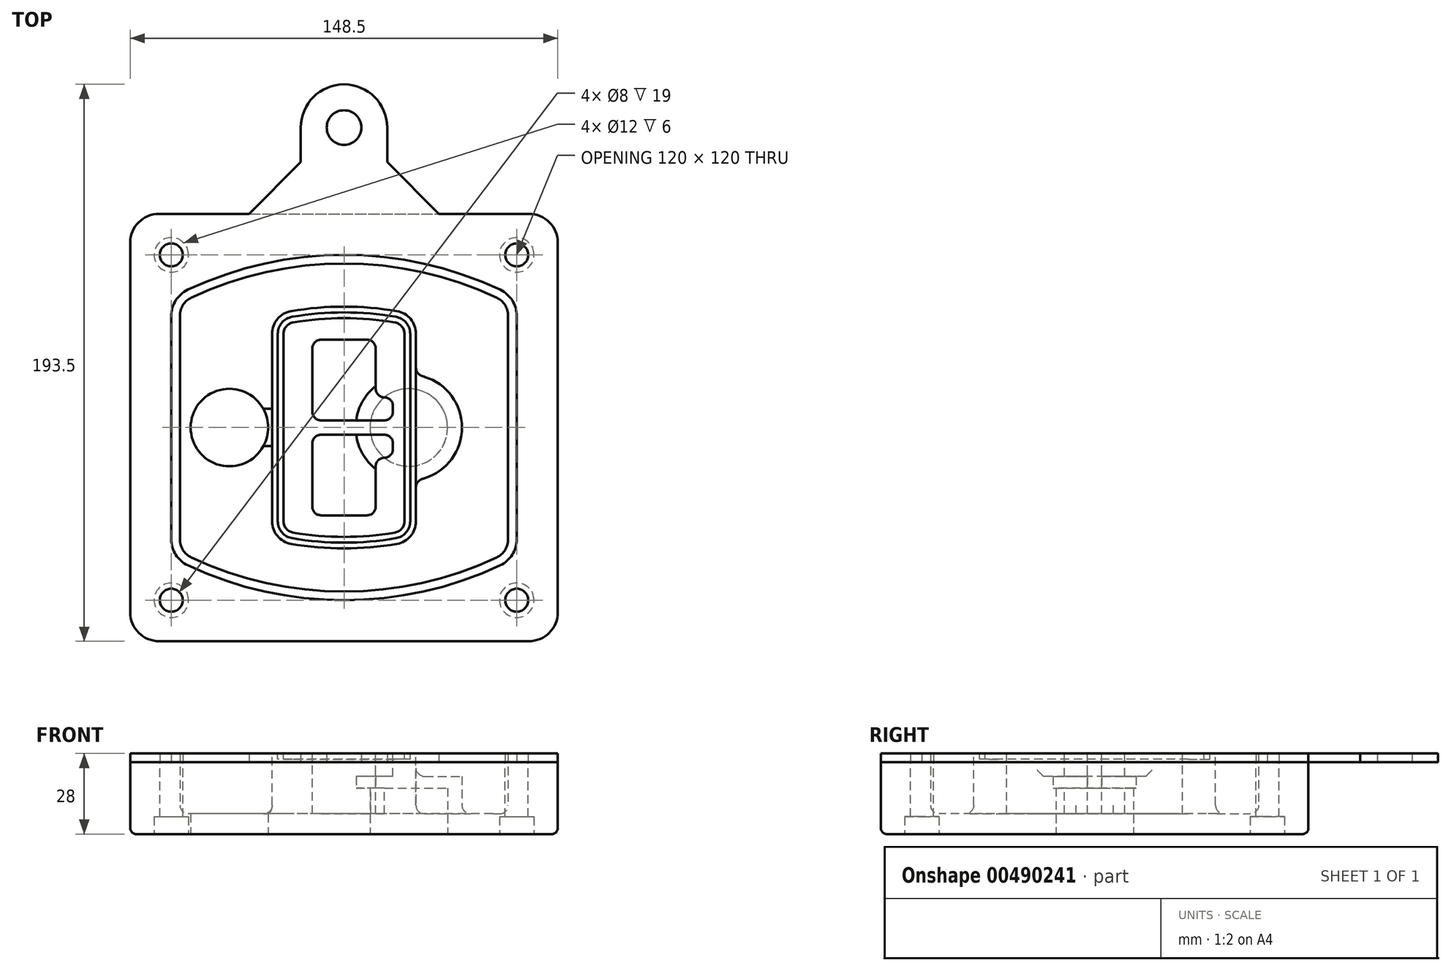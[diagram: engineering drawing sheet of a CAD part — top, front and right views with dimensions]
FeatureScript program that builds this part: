
annotation { "Feature Type Name" : "Feature", "Feature Type Description" : "" }
export const myFeature = defineFeature(function(context is Context, id is Id, definition is map)
    precondition{}
    {
        {
            var Q0;
            Q0=qCreatedBy(makeId("Top.planeOp"),FACE);
            var sketch = newSketch(context, id + "F0", { "sketchPlane" : qUnion([Q0])});
            skPoint(sketch, "E0.rect.middle", {"position": v(0, 0) * mm});
            skLineSegment(sketch, "E1.bottom", {"start": v(-64.25, -74.25) * mm, "end": v(64.25, -74.25) * mm});
            skLineSegment(sketch, "E1.top", {"start": v(-64.25, 74.25) * mm, "end": v(64.25, 74.25) * mm});
            skLineSegment(sketch, "E1.left", {"start": v(-74.25, -64.25) * mm, "end": v(-74.25, 64.25) * mm});
            skLineSegment(sketch, "E1.right", {"start": v(74.25, -64.25) * mm, "end": v(74.25, 64.25) * mm});
            skLineSegment(sketch, "E2", {"start": v(-74.25, 74.25) * mm, "end": v(74.25, -74.25) * mm, "construction": true});
            skLineSegment(sketch, "E3", {"start": v(74.25, 74.25) * mm, "end": v(-74.25, -74.25) * mm, "construction": true});
            skCircle(sketch, "E4", {"center": v(-60, 60) * mm, "radius": 4 * mm});
            skCircle(sketch, "E5", {"center": v(60, 60) * mm, "radius": 4 * mm});
            skCircle(sketch, "E6", {"center": v(60, -60) * mm, "radius": 4 * mm});
            skCircle(sketch, "E7", {"center": v(-60, -60) * mm, "radius": 4 * mm});
            skLineSegment(sketch, "E8", {"start": v(-60, 60) * mm, "end": v(60, 60) * mm, "construction": true});
            skLineSegment(sketch, "E9", {"start": v(60, 60) * mm, "end": v(60, -60) * mm, "construction": true});
            skLineSegment(sketch, "E10", {"start": v(60, -60) * mm, "end": v(-60, -60) * mm, "construction": true});
            skLineSegment(sketch, "E11", {"start": v(-60, -60) * mm, "end": v(-60, 60) * mm, "construction": true});
            skLineSegment(sketch, "E12", {"start": v(-60, 38.83) * mm, "end": v(-60, -38.83) * mm});
            skLineSegment(sketch, "E13", {"start": v(60, 38.83) * mm, "end": v(60, -38.83) * mm});
            skArc(sketch, "E14", {"start": v(54.26, 47.88) * mm, "mid": v(0, 60) * mm, "end": v(-54.26, 47.88) * mm});
            skArc(sketch, "E15", {"start": v(-54.26, -47.88) * mm, "mid": v(0, -60) * mm, "end": v(54.26, -47.88) * mm});
            skLineSegment(sketch, "E16", {"start": v(-60, 0) * mm, "end": v(60, 0) * mm, "construction": true});
            skPoint(sketch, "E17.visualSharp", {"position": v(-60, -45) * mm});
            skArc(sketch, "E17.filletArc", {"start": v(-60, -38.83) * mm, "mid": v(-58.44, -44.2) * mm, "end": v(-54.26, -47.88) * mm});
            skPoint(sketch, "E18.visualSharp", {"position": v(-60, 45) * mm});
            skArc(sketch, "E18.filletArc", {"start": v(-54.26, 47.88) * mm, "mid": v(-58.44, 44.2) * mm, "end": v(-60, 38.83) * mm});
            skPoint(sketch, "E19.visualSharp", {"position": v(60, 45) * mm});
            skArc(sketch, "E19.filletArc", {"start": v(60, 38.83) * mm, "mid": v(58.44, 44.2) * mm, "end": v(54.26, 47.88) * mm});
            skPoint(sketch, "E20.visualSharp", {"position": v(60, -45) * mm});
            skArc(sketch, "E20.filletArc", {"start": v(54.26, -47.88) * mm, "mid": v(58.44, -44.2) * mm, "end": v(60, -38.83) * mm});
            skPoint(sketch, "E21.visualSharp", {"position": v(-74.25, 74.25) * mm});
            skArc(sketch, "E21.filletArc", {"start": v(-64.25, 74.25) * mm, "mid": v(-71.32, 71.32) * mm, "end": v(-74.25, 64.25) * mm});
            skPoint(sketch, "E22.visualSharp", {"position": v(74.25, 74.25) * mm});
            skArc(sketch, "E22.filletArc", {"start": v(74.25, 64.25) * mm, "mid": v(71.32, 71.32) * mm, "end": v(64.25, 74.25) * mm});
            skPoint(sketch, "E23.visualSharp", {"position": v(74.25, -74.25) * mm});
            skArc(sketch, "E23.filletArc", {"start": v(64.25, -74.25) * mm, "mid": v(71.32, -71.32) * mm, "end": v(74.25, -64.25) * mm});
            skPoint(sketch, "E24.visualSharp", {"position": v(-74.25, -74.25) * mm});
            skArc(sketch, "E24.filletArc", {"start": v(-74.25, -64.25) * mm, "mid": v(-71.32, -71.32) * mm, "end": v(-64.25, -74.25) * mm});
            skArc(sketch, "E25.0", {"start": v(57, 38.83) * mm, "mid": v(55.9, 42.58) * mm, "end": v(52.98, 45.17) * mm});
            skLineSegment(sketch, "E25.1", {"start": v(57, 38.83) * mm, "end": v(57, -38.83) * mm});
            skArc(sketch, "E25.2", {"start": v(52.98, -45.17) * mm, "mid": v(55.9, -42.58) * mm, "end": v(57, -38.83) * mm});
            skArc(sketch, "E25.3", {"start": v(-52.98, -45.17) * mm, "mid": v(0, -57) * mm, "end": v(52.98, -45.17) * mm});
            skArc(sketch, "E25.4", {"start": v(-57, -38.83) * mm, "mid": v(-55.9, -42.58) * mm, "end": v(-52.98, -45.17) * mm});
            skArc(sketch, "E25.5", {"start": v(52.98, 45.17) * mm, "mid": v(0, 57) * mm, "end": v(-52.98, 45.17) * mm});
            skLineSegment(sketch, "E25.6", {"start": v(-57, 38.83) * mm, "end": v(-57, -38.83) * mm});
            skArc(sketch, "E25.7", {"start": v(-52.98, 45.17) * mm, "mid": v(-55.9, 42.58) * mm, "end": v(-57, 38.83) * mm});
            skArc(sketch, "E26.0", {"start": v(-55.96, 51.5) * mm, "mid": v(-61.82, 46.33) * mm, "end": v(-64, 38.83) * mm});
            skArc(sketch, "E26.1", {"start": v(55.96, 51.5) * mm, "mid": v(0, 64) * mm, "end": v(-55.96, 51.5) * mm});
            skArc(sketch, "E26.2", {"start": v(64, 38.83) * mm, "mid": v(61.82, 46.33) * mm, "end": v(55.96, 51.5) * mm});
            skLineSegment(sketch, "E26.3", {"start": v(64, 38.83) * mm, "end": v(64, -38.83) * mm});
            skArc(sketch, "E26.4", {"start": v(55.96, -51.5) * mm, "mid": v(61.82, -46.33) * mm, "end": v(64, -38.83) * mm});
            skLineSegment(sketch, "E26.5", {"start": v(-64, 38.83) * mm, "end": v(-64, -38.83) * mm});
            skArc(sketch, "E26.6", {"start": v(-55.96, -51.5) * mm, "mid": v(0, -64) * mm, "end": v(55.96, -51.5) * mm});
            skArc(sketch, "E26.7", {"start": v(-64, -38.83) * mm, "mid": v(-61.82, -46.33) * mm, "end": v(-55.96, -51.5) * mm});
            skSolve(sketch);
        }
        {
            var Q0;
            Q0=makeQuery(id+"F0.imprint","IMPRINT",FACE,{"disambiguationData":[TD([[makeQuery(id+"F0.imprint","IMPRINT",EDGE,{"derivedFrom":sQuery(id+"F0.wireOp",EDGE,"E1.bottom")}),1.0]])]});
            var Q1;
            Q1=makeQuery(id+"F0.imprint","IMPRINT",FACE,{"disambiguationData":[TD([[makeQuery(id+"F0.imprint","IMPRINT",EDGE,{"derivedFrom":sQuery(id+"F0.wireOp",EDGE,"E12")}),1.0]])]});
            var Q2;
            Q2=makeQuery(id+"F0.imprint","IMPRINT",FACE,{"disambiguationData":[TD([[makeQuery(id+"F0.imprint","IMPRINT",EDGE,{"derivedFrom":sQuery(id+"F0.wireOp",EDGE,"E25.0")}),1.0]])]});
            var Q3;
            Q3=makeQuery(id+"F0.imprint","IMPRINT",FACE,{"disambiguationData":[TD([[makeQuery(id+"F0.imprint","IMPRINT",EDGE,{"derivedFrom":sQuery(id+"F0.wireOp",EDGE,"E12")}),-1.0]])]});
            extrude(context, id + "F1", {"entities" : qUnion([Q0, Q1, Q2, Q3]), "oppositeDirection" : true, "depth" : 25 * mm});
        }
        {
            var Q0;
            Q0=makeQuery(id+"F0.imprint","IMPRINT",FACE,{"disambiguationData":[TD([[makeQuery(id+"F0.imprint","IMPRINT",EDGE,{"derivedFrom":sQuery(id+"F0.wireOp",EDGE,"E12")}),1.0]])]});
            extrude(context, id + "F2", {"entities" : qUnion([Q0]), "operationType" : NewBodyOperationType.ADD, "depth" : 3 * mm});
        }
        {
            var Q0;
            Q0=makeQuery(id+"F0.imprint","IMPRINT",FACE,{"disambiguationData":[TD([[makeQuery(id+"F0.imprint","IMPRINT",EDGE,{"derivedFrom":sQuery(id+"F0.wireOp",EDGE,"E25.0")}),1.0]])]});
            extrude(context, id + "F3", {"entities" : qUnion([Q0]), "operationType" : NewBodyOperationType.REMOVE, "oppositeDirection" : true, "depth" : 18 * mm});
        }
        {
            var Q0;
            Q0=makeQuery(id+"F2.opExtrude","CAP_FACE",FACE,{"disambiguationData":[OSD([sQuery(id+"F0.wireOp",EDGE,"E12"),sQuery(id+"F0.wireOp",EDGE,"E13"),sQuery(id+"F0.wireOp",EDGE,"E14"),sQuery(id+"F0.wireOp",EDGE,"E15"),sQuery(id+"F0.wireOp",EDGE,"E17.filletArc"),sQuery(id+"F0.wireOp",EDGE,"E18.filletArc"),sQuery(id+"F0.wireOp",EDGE,"E19.filletArc"),sQuery(id+"F0.wireOp",EDGE,"E20.filletArc"),sQuery(id+"F0.wireOp",EDGE,"E25.0"),sQuery(id+"F0.wireOp",EDGE,"E25.1"),sQuery(id+"F0.wireOp",EDGE,"E25.2"),sQuery(id+"F0.wireOp",EDGE,"E25.3"),sQuery(id+"F0.wireOp",EDGE,"E25.4"),sQuery(id+"F0.wireOp",EDGE,"E25.5"),sQuery(id+"F0.wireOp",EDGE,"E25.6"),sQuery(id+"F0.wireOp",EDGE,"E25.7")])],"isStart":false});
            var sketch = newSketch(context, id + "F4", { "sketchPlane" : qUnion([Q0])});
            skArc(sketch, "E27.0", {"start": v(-18.34, -40.45) * mm, "mid": v(0, -42) * mm, "end": v(18.34, -40.45) * mm});
            skArc(sketch, "E28.0", {"start": v(18.34, 40.45) * mm, "mid": v(0, 42) * mm, "end": v(-18.34, 40.45) * mm});
            skLineSegment(sketch, "E29", {"start": v(-25, 32.57) * mm, "end": v(-25, -32.57) * mm});
            skLineSegment(sketch, "E30", {"start": v(25, 32.57) * mm, "end": v(25, -32.57) * mm});
            skLineSegment(sketch, "E31", {"start": v(-25, 39.1) * mm, "end": v(25, 39.1) * mm, "construction": true});
            skLineSegment(sketch, "E32", {"start": v(-25, -39.1) * mm, "end": v(25, -39.1) * mm, "construction": true});
            skPoint(sketch, "E33.visualSharp", {"position": v(-25, 39.1) * mm});
            skArc(sketch, "E33.filletArc", {"start": v(-18.34, 40.45) * mm, "mid": v(-23.11, 37.73) * mm, "end": v(-25, 32.57) * mm});
            skPoint(sketch, "E34.visualSharp", {"position": v(25, 39.1) * mm});
            skArc(sketch, "E34.filletArc", {"start": v(25, 32.57) * mm, "mid": v(23.11, 37.73) * mm, "end": v(18.34, 40.45) * mm});
            skPoint(sketch, "E35.visualSharp", {"position": v(25, -39.1) * mm});
            skArc(sketch, "E35.filletArc", {"start": v(18.34, -40.45) * mm, "mid": v(23.11, -37.73) * mm, "end": v(25, -32.57) * mm});
            skPoint(sketch, "E36.visualSharp", {"position": v(-25, -39.1) * mm});
            skArc(sketch, "E36.filletArc", {"start": v(-25, -32.57) * mm, "mid": v(-23.11, -37.73) * mm, "end": v(-18.34, -40.45) * mm});
            skArc(sketch, "E37.0", {"start": v(52.98, 45.17) * mm, "mid": v(0, 57) * mm, "end": v(-52.98, 45.17) * mm});
            skArc(sketch, "E37.1", {"start": v(-52.98, 45.17) * mm, "mid": v(-55.9, 42.58) * mm, "end": v(-57, 38.83) * mm});
            skLineSegment(sketch, "E37.2", {"start": v(-57, 38.83) * mm, "end": v(-57, -38.83) * mm});
            skArc(sketch, "E37.3", {"start": v(-57, -38.83) * mm, "mid": v(-55.9, -42.58) * mm, "end": v(-52.98, -45.17) * mm});
            skArc(sketch, "E37.4", {"start": v(-52.98, -45.17) * mm, "mid": v(0, -57) * mm, "end": v(52.98, -45.17) * mm});
            skArc(sketch, "E37.5", {"start": v(52.98, -45.17) * mm, "mid": v(55.9, -42.58) * mm, "end": v(57, -38.83) * mm});
            skLineSegment(sketch, "E37.6", {"start": v(57, 38.83) * mm, "end": v(57, -38.83) * mm});
            skArc(sketch, "E37.7", {"start": v(57, 38.83) * mm, "mid": v(55.9, 42.58) * mm, "end": v(52.98, 45.17) * mm});
            skLineSegment(sketch, "E38.0", {"start": v(23, 32.57) * mm, "end": v(23, -32.57) * mm});
            skArc(sketch, "E38.1", {"start": v(18, -38.48) * mm, "mid": v(21.58, -36.44) * mm, "end": v(23, -32.57) * mm});
            skArc(sketch, "E38.2", {"start": v(-18, -38.48) * mm, "mid": v(0, -40) * mm, "end": v(18, -38.48) * mm});
            skArc(sketch, "E38.3", {"start": v(-23, -32.57) * mm, "mid": v(-21.58, -36.44) * mm, "end": v(-18, -38.48) * mm});
            skLineSegment(sketch, "E38.4", {"start": v(-23, 32.57) * mm, "end": v(-23, -32.57) * mm});
            skArc(sketch, "E38.5", {"start": v(23, 32.57) * mm, "mid": v(21.58, 36.44) * mm, "end": v(18, 38.48) * mm});
            skArc(sketch, "E38.6", {"start": v(-18, 38.48) * mm, "mid": v(-21.58, 36.44) * mm, "end": v(-23, 32.57) * mm});
            skArc(sketch, "E38.7", {"start": v(18, 38.48) * mm, "mid": v(0, 40) * mm, "end": v(-18, 38.48) * mm});
            skArc(sketch, "E39.0", {"start": v(21, 32.57) * mm, "mid": v(20.06, 35.15) * mm, "end": v(17.67, 36.5) * mm});
            skLineSegment(sketch, "E39.1", {"start": v(21, 32.57) * mm, "end": v(21, -32.57) * mm});
            skArc(sketch, "E39.2", {"start": v(17.67, -36.5) * mm, "mid": v(20.06, -35.15) * mm, "end": v(21, -32.57) * mm});
            skArc(sketch, "E39.3", {"start": v(-17.67, -36.5) * mm, "mid": v(0, -38) * mm, "end": v(17.67, -36.5) * mm});
            skArc(sketch, "E39.4", {"start": v(-21, -32.57) * mm, "mid": v(-20.06, -35.15) * mm, "end": v(-17.67, -36.5) * mm});
            skArc(sketch, "E39.5", {"start": v(17.67, 36.5) * mm, "mid": v(0, 38) * mm, "end": v(-17.67, 36.5) * mm});
            skLineSegment(sketch, "E39.6", {"start": v(-21, 32.57) * mm, "end": v(-21, -32.57) * mm});
            skArc(sketch, "E39.7", {"start": v(-17.67, 36.5) * mm, "mid": v(-20.06, 35.15) * mm, "end": v(-21, 32.57) * mm});
            skLineSegment(sketch, "E40", {"start": v(-25, 0) * mm, "end": v(25, 0) * mm, "construction": true});
            skLineSegment(sketch, "E41", {"start": v(-11, 5.5) * mm, "end": v(-11, 27.5) * mm});
            skLineSegment(sketch, "E42", {"start": v(-8, 30.5) * mm, "end": v(8, 30.5) * mm});
            skLineSegment(sketch, "E43", {"start": v(11, 27.5) * mm, "end": v(11, 13.5) * mm});
            skLineSegment(sketch, "E44", {"start": v(14, 10.5) * mm, "end": v(14, 10.5) * mm});
            skLineSegment(sketch, "E45", {"start": v(17, 7.5) * mm, "end": v(17, 5.5) * mm});
            skLineSegment(sketch, "E46", {"start": v(14, 2.5) * mm, "end": v(-8, 2.5) * mm});
            skPoint(sketch, "E47.visualSharp", {"position": v(-11, 30.5) * mm});
            skArc(sketch, "E47.filletArc", {"start": v(-8, 30.5) * mm, "mid": v(-10.12, 29.62) * mm, "end": v(-11, 27.5) * mm});
            skPoint(sketch, "E48.visualSharp", {"position": v(11, 30.5) * mm});
            skArc(sketch, "E48.filletArc", {"start": v(11, 27.5) * mm, "mid": v(10.12, 29.62) * mm, "end": v(8, 30.5) * mm});
            skPoint(sketch, "E49.visualSharp", {"position": v(11, 10.5) * mm});
            skArc(sketch, "E49.filletArc", {"start": v(11, 13.5) * mm, "mid": v(11.88, 11.38) * mm, "end": v(14, 10.5) * mm});
            skPoint(sketch, "E50.visualSharp", {"position": v(17, 10.5) * mm});
            skArc(sketch, "E50.filletArc", {"start": v(17, 7.5) * mm, "mid": v(16.12, 9.62) * mm, "end": v(14, 10.5) * mm});
            skPoint(sketch, "E51.visualSharp", {"position": v(17, 2.5) * mm});
            skArc(sketch, "E51.filletArc", {"start": v(14, 2.5) * mm, "mid": v(16.12, 3.38) * mm, "end": v(17, 5.5) * mm});
            skPoint(sketch, "E52.visualSharp", {"position": v(-11, 2.5) * mm});
            skArc(sketch, "E52.filletArc", {"start": v(-11, 5.5) * mm, "mid": v(-10.12, 3.38) * mm, "end": v(-8, 2.5) * mm});
            skLineSegment(sketch, "E53.0.MirrorCS", {"start": v(14, -2.5) * mm, "end": v(-8, -2.5) * mm});
            skArc(sketch, "E54.0.MirrorCS", {"start": v(-11, -5.5) * mm, "mid": v(-10.12, -3.38) * mm, "end": v(-8, -2.5) * mm});
            skLineSegment(sketch, "E55.0.MirrorCS", {"start": v(-11, -5.5) * mm, "end": v(-11, -27.5) * mm});
            skArc(sketch, "E56.0.MirrorCS", {"start": v(-8, -30.5) * mm, "mid": v(-10.12, -29.62) * mm, "end": v(-11, -27.5) * mm});
            skLineSegment(sketch, "E57.0.MirrorCS", {"start": v(-8, -30.5) * mm, "end": v(8, -30.5) * mm});
            skArc(sketch, "E58.0.MirrorCS", {"start": v(11, -27.5) * mm, "mid": v(10.12, -29.62) * mm, "end": v(8, -30.5) * mm});
            skLineSegment(sketch, "E59.0.MirrorCS", {"start": v(11, -27.5) * mm, "end": v(11, -13.5) * mm});
            skArc(sketch, "E60.0.MirrorCS", {"start": v(11, -13.5) * mm, "mid": v(11.88, -11.38) * mm, "end": v(14, -10.5) * mm});
            skArc(sketch, "E61.0.MirrorCS", {"start": v(17, -7.5) * mm, "mid": v(16.12, -9.62) * mm, "end": v(14, -10.5) * mm});
            skLineSegment(sketch, "E62.0.MirrorCS", {"start": v(17, -7.5) * mm, "end": v(17, -5.5) * mm});
            skArc(sketch, "E63.0.MirrorCS", {"start": v(14, -2.5) * mm, "mid": v(16.12, -3.38) * mm, "end": v(17, -5.5) * mm});
            skSolve(sketch);
        }
        {
            var Q0;
            Q0=makeQuery(id+"F4.imprint","IMPRINT",FACE,{"disambiguationData":[TD([[makeQuery(id+"F4.imprint","IMPRINT",EDGE,{"derivedFrom":sQuery(id+"F4.wireOp",EDGE,"E27.0")}),1.0]])]});
            var Q1;
            Q1=makeQuery(id+"F4.imprint","IMPRINT",FACE,{"disambiguationData":[TD([[makeQuery(id+"F4.imprint","IMPRINT",EDGE,{"derivedFrom":sQuery(id+"F4.wireOp",EDGE,"E38.0")}),-1.0]])]});
            var Q2;
            Q2=makeQuery(id+"F4.imprint","IMPRINT",FACE,{"disambiguationData":[TD([[makeQuery(id+"F4.imprint","IMPRINT",EDGE,{"derivedFrom":sQuery(id+"F4.wireOp",EDGE,"E39.0")}),1.0]])]});
            extrude(context, id + "F5", {"entities" : qUnion([Q0, Q1, Q2]), "operationType" : NewBodyOperationType.ADD, "endBound" : BoundingType.UP_TO_NEXT, "oppositeDirection" : true, "depth" : 25 * mm});
        }
        {
            var Q0;
            Q0=makeQuery(id+"F4.imprint","IMPRINT",FACE,{"disambiguationData":[TD([[makeQuery(id+"F4.imprint","IMPRINT",EDGE,{"derivedFrom":sQuery(id+"F4.wireOp",EDGE,"E38.0")}),-1.0]])]});
            extrude(context, id + "F6", {"entities" : qUnion([Q0]), "operationType" : NewBodyOperationType.REMOVE, "oppositeDirection" : true, "depth" : 2 * mm});
        }
        {
            var Q0;
            Q0=makeQuery(id+"F1.opExtrude","CAP_FACE",FACE,{"disambiguationData":[OSD([sQuery(id+"F0.wireOp",EDGE,"E1.bottom"),sQuery(id+"F0.wireOp",EDGE,"E1.top"),sQuery(id+"F0.wireOp",EDGE,"E1.left"),sQuery(id+"F0.wireOp",EDGE,"E1.right"),sQuery(id+"F0.wireOp",EDGE,"E4"),sQuery(id+"F0.wireOp",EDGE,"E5"),sQuery(id+"F0.wireOp",EDGE,"E6"),sQuery(id+"F0.wireOp",EDGE,"E7"),sQuery(id+"F0.wireOp",EDGE,"E21.filletArc"),sQuery(id+"F0.wireOp",EDGE,"E22.filletArc"),sQuery(id+"F0.wireOp",EDGE,"E23.filletArc"),sQuery(id+"F0.wireOp",EDGE,"E24.filletArc")])],"isStart":false});
            var sketch = newSketch(context, id + "F7", { "sketchPlane" : qUnion([Q0])});
            skCircle(sketch, "E64", {"center": v(22.5, 0) * mm, "radius": 13.47 * mm});
            skCircle(sketch, "E65", {"center": v(-39.81, 0) * mm, "radius": 13.47 * mm});
            skLineSegment(sketch, "E66", {"start": v(74.25, 0) * mm, "end": v(-74.25, 0) * mm});
            skCircle(sketch, "E67", {"center": v(22.5, 0) * mm, "radius": 18.47 * mm});
            skCircle(sketch, "E68", {"center": v(60, -60) * mm, "radius": 6 * mm});
            skCircle(sketch, "E69", {"center": v(-60, -60) * mm, "radius": 6 * mm});
            skCircle(sketch, "E70", {"center": v(-60, 60) * mm, "radius": 6 * mm});
            skCircle(sketch, "E71", {"center": v(60, 60) * mm, "radius": 6 * mm});
            skSolve(sketch);
        }
        {
            var Q0;
            {var subQ1=sQuery(id+"F7.wireOp",EDGE,"E66");var subQ4=sQuery(id+"F7.wireOp",EDGE,"E64");var subQ6=makeQuery(id+"F7.imprint","INTERSECT",VERTEX,{"disambiguationData":[OD(0.0)],"derivedFrom":[subQ4,subQ1]});Q0=makeQuery(id+"F7.imprint","IMPRINT",FACE,{"disambiguationData":[TD([[makeQuery(id+"F7.imprint","IMPRINT",EDGE,{"disambiguationData":[TD([[subQ6,-1.0]])],"derivedFrom":subQ4}),-1.0]])]});}
            var Q1;
            {var subQ0=sQuery(id+"F7.wireOp",EDGE,"E66");var subQ1=sQuery(id+"F7.wireOp",EDGE,"E64");var subQ3=makeQuery(id+"F7.imprint","INTERSECT",VERTEX,{"disambiguationData":[OD(0.0)],"derivedFrom":[subQ1,subQ0]});Q1=makeQuery(id+"F7.imprint","IMPRINT",FACE,{"disambiguationData":[TD([[makeQuery(id+"F7.imprint","IMPRINT",EDGE,{"disambiguationData":[TD([[subQ3,-1.0]])],"derivedFrom":subQ1}),1.0]])]});}
            var Q2;
            {var subQ0=sQuery(id+"F7.wireOp",EDGE,"E66");var subQ1=sQuery(id+"F7.wireOp",EDGE,"E64");var subQ3=makeQuery(id+"F7.imprint","INTERSECT",VERTEX,{"disambiguationData":[OD(0.0)],"derivedFrom":[subQ1,subQ0]});Q2=makeQuery(id+"F7.imprint","IMPRINT",FACE,{"disambiguationData":[TD([[makeQuery(id+"F7.imprint","IMPRINT",EDGE,{"disambiguationData":[TD([[subQ3,1.0]])],"derivedFrom":subQ1}),1.0]])]});}
            var Q3;
            {var subQ1=sQuery(id+"F7.wireOp",EDGE,"E66");var subQ4=sQuery(id+"F7.wireOp",EDGE,"E64");var subQ6=makeQuery(id+"F7.imprint","INTERSECT",VERTEX,{"disambiguationData":[OD(0.0)],"derivedFrom":[subQ4,subQ1]});Q3=makeQuery(id+"F7.imprint","IMPRINT",FACE,{"disambiguationData":[TD([[makeQuery(id+"F7.imprint","IMPRINT",EDGE,{"disambiguationData":[TD([[subQ6,1.0]])],"derivedFrom":subQ4}),-1.0]])]});}
            extrude(context, id + "F8", {"entities" : qUnion([Q0, Q1, Q2, Q3]), "operationType" : NewBodyOperationType.ADD, "oppositeDirection" : true, "depth" : 20 * mm});
        }
        {
            var Q0;
            {var subQ0=sQuery(id+"F7.wireOp",EDGE,"E66");var subQ1=sQuery(id+"F7.wireOp",EDGE,"E64");var subQ3=makeQuery(id+"F7.imprint","INTERSECT",VERTEX,{"disambiguationData":[OD(0.0)],"derivedFrom":[subQ1,subQ0]});Q0=makeQuery(id+"F7.imprint","IMPRINT",FACE,{"disambiguationData":[TD([[makeQuery(id+"F7.imprint","IMPRINT",EDGE,{"disambiguationData":[TD([[subQ3,-1.0]])],"derivedFrom":subQ1}),1.0]])]});}
            var Q1;
            {var subQ0=sQuery(id+"F7.wireOp",EDGE,"E66");var subQ1=sQuery(id+"F7.wireOp",EDGE,"E64");var subQ3=makeQuery(id+"F7.imprint","INTERSECT",VERTEX,{"disambiguationData":[OD(0.0)],"derivedFrom":[subQ1,subQ0]});Q1=makeQuery(id+"F7.imprint","IMPRINT",FACE,{"disambiguationData":[TD([[makeQuery(id+"F7.imprint","IMPRINT",EDGE,{"disambiguationData":[TD([[subQ3,1.0]])],"derivedFrom":subQ1}),1.0]])]});}
            extrude(context, id + "F9", {"entities" : qUnion([Q0, Q1]), "operationType" : NewBodyOperationType.REMOVE, "oppositeDirection" : true, "depth" : 16 * mm});
        }
        {
            var Q0;
            {var subQ0=sQuery(id+"F7.wireOp",EDGE,"E66");var subQ1=sQuery(id+"F7.wireOp",EDGE,"E65");var subQ3=makeQuery(id+"F7.imprint","INTERSECT",VERTEX,{"disambiguationData":[OD(0.0)],"derivedFrom":[subQ1,subQ0]});Q0=makeQuery(id+"F7.imprint","IMPRINT",FACE,{"disambiguationData":[TD([[makeQuery(id+"F7.imprint","IMPRINT",EDGE,{"disambiguationData":[TD([[subQ3,-1.0]])],"derivedFrom":subQ1}),1.0]])]});}
            var Q1;
            {var subQ0=sQuery(id+"F7.wireOp",EDGE,"E66");var subQ1=sQuery(id+"F7.wireOp",EDGE,"E65");var subQ3=makeQuery(id+"F7.imprint","INTERSECT",VERTEX,{"disambiguationData":[OD(0.0)],"derivedFrom":[subQ1,subQ0]});Q1=makeQuery(id+"F7.imprint","IMPRINT",FACE,{"disambiguationData":[TD([[makeQuery(id+"F7.imprint","IMPRINT",EDGE,{"disambiguationData":[TD([[subQ3,1.0]])],"derivedFrom":subQ1}),1.0]])]});}
            extrude(context, id + "F10", {"entities" : qUnion([Q0, Q1]), "operationType" : NewBodyOperationType.REMOVE, "oppositeDirection" : true, "depth" : 25 * mm});
        }
        {
            var Q0;
            Q0=makeQuery(id+"F7.imprint","IMPRINT",FACE,{"disambiguationData":[TD([[makeQuery(id+"F7.imprint","IMPRINT",EDGE,{"derivedFrom":sQuery(id+"F7.wireOp",EDGE,"E68")}),1.0]])]});
            var Q1;
            Q1=makeQuery(id+"F7.imprint","IMPRINT",FACE,{"disambiguationData":[TD([[makeQuery(id+"F7.imprint","IMPRINT",EDGE,{"derivedFrom":makeQuery(id+"F1.opExtrude","CAP_EDGE",EDGE,{"disambiguationData":[OSD([sQuery(id+"F0.wireOp",EDGE,"E5")])],"isStart":false})}),-1.0]])]});
            var Q2;
            Q2=makeQuery(id+"F7.imprint","IMPRINT",FACE,{"disambiguationData":[TD([[makeQuery(id+"F7.imprint","IMPRINT",EDGE,{"derivedFrom":sQuery(id+"F7.wireOp",EDGE,"E69")}),1.0]])]});
            var Q3;
            Q3=makeQuery(id+"F7.imprint","IMPRINT",FACE,{"disambiguationData":[TD([[makeQuery(id+"F7.imprint","IMPRINT",EDGE,{"derivedFrom":makeQuery(id+"F1.opExtrude","CAP_EDGE",EDGE,{"disambiguationData":[OSD([sQuery(id+"F0.wireOp",EDGE,"E4")])],"isStart":false})}),-1.0]])]});
            var Q4;
            Q4=makeQuery(id+"F7.imprint","IMPRINT",FACE,{"disambiguationData":[TD([[makeQuery(id+"F7.imprint","IMPRINT",EDGE,{"derivedFrom":sQuery(id+"F7.wireOp",EDGE,"E70")}),1.0]])]});
            var Q5;
            Q5=makeQuery(id+"F7.imprint","IMPRINT",FACE,{"disambiguationData":[TD([[makeQuery(id+"F7.imprint","IMPRINT",EDGE,{"derivedFrom":makeQuery(id+"F1.opExtrude","CAP_EDGE",EDGE,{"disambiguationData":[OSD([sQuery(id+"F0.wireOp",EDGE,"E7")])],"isStart":false})}),-1.0]])]});
            var Q6;
            Q6=makeQuery(id+"F7.imprint","IMPRINT",FACE,{"disambiguationData":[TD([[makeQuery(id+"F7.imprint","IMPRINT",EDGE,{"derivedFrom":sQuery(id+"F7.wireOp",EDGE,"E71")}),1.0]])]});
            var Q7;
            Q7=makeQuery(id+"F7.imprint","IMPRINT",FACE,{"disambiguationData":[TD([[makeQuery(id+"F7.imprint","IMPRINT",EDGE,{"derivedFrom":makeQuery(id+"F1.opExtrude","CAP_EDGE",EDGE,{"disambiguationData":[OSD([sQuery(id+"F0.wireOp",EDGE,"E6")])],"isStart":false})}),-1.0]])]});
            extrude(context, id + "F11", {"entities" : qUnion([Q0, Q1, Q2, Q3, Q4, Q5, Q6, Q7]), "operationType" : NewBodyOperationType.REMOVE, "oppositeDirection" : true, "depth" : 6 * mm});
        }
        {
            var Q0;
            Q0=makeQuery(id+"F9.boolean.opBoolean","COPY",FACE,{"derivedFrom":makeQuery(id+"F9.opExtrude","CAP_FACE",FACE,{"disambiguationData":[OSD([sQuery(id+"F7.wireOp",EDGE,"E64")])],"isStart":false})});
            var sketch = newSketch(context, id + "F12", { "sketchPlane" : qUnion([Q0])});
            skArc(sketch, "E72.0", {"start": v(11, 14.45) * mm, "mid": v(6.45, 9.13) * mm, "end": v(4.2, 2.5) * mm});
            skArc(sketch, "E72.1", {"start": v(4.2, -2.5) * mm, "mid": v(6.45, -9.13) * mm, "end": v(11, -14.45) * mm});
            skLineSegment(sketch, "E73", {"start": v(4.2, -2.5) * mm, "end": v(14, -2.5) * mm});
            skLineSegment(sketch, "E74.0", {"start": v(14, 2.5) * mm, "end": v(4.2, 2.5) * mm});
            skArc(sketch, "E74.1", {"start": v(14, 2.5) * mm, "mid": v(16.12, 3.38) * mm, "end": v(17, 5.5) * mm});
            skLineSegment(sketch, "E74.2", {"start": v(17, 7.5) * mm, "end": v(17, 5.5) * mm});
            skArc(sketch, "E74.3", {"start": v(17, 7.5) * mm, "mid": v(16.12, 9.62) * mm, "end": v(14, 10.5) * mm});
            skArc(sketch, "E74.4", {"start": v(11, 13.5) * mm, "mid": v(11.88, 11.38) * mm, "end": v(14, 10.5) * mm});
            skLineSegment(sketch, "E74.5", {"start": v(11, 14.45) * mm, "end": v(11, 13.5) * mm});
            skLineSegment(sketch, "E74.7", {"start": v(14, -2.5) * mm, "end": v(4.2, -2.5) * mm});
            skArc(sketch, "E74.8", {"start": v(14, -2.5) * mm, "mid": v(16.12, -3.38) * mm, "end": v(17, -5.5) * mm});
            skLineSegment(sketch, "E74.9", {"start": v(17, -7.5) * mm, "end": v(17, -5.5) * mm});
            skArc(sketch, "E74.10", {"start": v(17, -7.5) * mm, "mid": v(16.12, -9.62) * mm, "end": v(14, -10.5) * mm});
            skArc(sketch, "E74.11", {"start": v(11, -13.5) * mm, "mid": v(11.88, -11.38) * mm, "end": v(14, -10.5) * mm});
            skLineSegment(sketch, "E74.12", {"start": v(11, -14.45) * mm, "end": v(11, -13.5) * mm});
            skPoint(sketch, "E75.orphan", {"position": v(11, -27.5) * mm});
            skPoint(sketch, "E76.orphan", {"position": v(-8, -2.5) * mm});
            skPoint(sketch, "E77.orphan", {"position": v(-8, 2.5) * mm});
            skPoint(sketch, "E78.orphan", {"position": v(11, 27.5) * mm});
            skSolve(sketch);
        }
        {
            var Q0;
            {var subQ7=sQuery(id+"F12.wireOp",EDGE,"E72.0");var subQ14=sQuery(id+"F12.wireOp",EDGE,"E72.1");var subQ16=sQuery(id+"F12.wireOp",EDGE,"E74.1");var subQ18=sQuery(id+"F12.wireOp",EDGE,"E74.8");Q0=qUnion([makeQuery(id+"F12.imprint","IMPRINT",FACE,{"disambiguationData":[TD([[makeQuery(id+"F12.imprint","IMPRINT",EDGE,{"derivedFrom":subQ7}),1.0]])]}),makeQuery(id+"F12.imprint","IMPRINT",FACE,{"disambiguationData":[TD([[makeQuery(id+"F12.imprint","IMPRINT",EDGE,{"derivedFrom":subQ14}),1.0]])]}),makeQuery(id+"F12.imprint","IMPRINT",FACE,{"disambiguationData":[TD([[makeQuery(id+"F12.imprint","IMPRINT",EDGE,{"derivedFrom":subQ16}),1.0]])]}),makeQuery(id+"F12.imprint","IMPRINT",FACE,{"disambiguationData":[TD([[makeQuery(id+"F12.imprint","IMPRINT",EDGE,{"derivedFrom":subQ18}),-1.0]])]})]);}
            var Q1;
            Q1=makeQuery(id+"F5.boolean.opBoolean","SPLIT",FACE,{"disambiguationData":[TD([makeQuery(id+"F5.opExtrude","SWEPT_FACE",FACE,{"disambiguationData":[OSD([sQuery(id+"F4.wireOp",EDGE,"E41")])]})])],"derivedFrom":makeQuery(id+"F3.boolean.opBoolean","COPY",FACE,{"derivedFrom":makeQuery(id+"F3.opExtrude","CAP_FACE",FACE,{"disambiguationData":[OSD([sQuery(id+"F0.wireOp",EDGE,"E25.0"),sQuery(id+"F0.wireOp",EDGE,"E25.1"),sQuery(id+"F0.wireOp",EDGE,"E25.2"),sQuery(id+"F0.wireOp",EDGE,"E25.3"),sQuery(id+"F0.wireOp",EDGE,"E25.4"),sQuery(id+"F0.wireOp",EDGE,"E25.5"),sQuery(id+"F0.wireOp",EDGE,"E25.6"),sQuery(id+"F0.wireOp",EDGE,"E25.7")])],"isStart":false})})});
            extrude(context, id + "F13", {"entities" : qUnion([Q0]), "operationType" : NewBodyOperationType.REMOVE, "endBound" : BoundingType.UP_TO_SURFACE, "endBoundEntityFace" : qUnion([Q1]), "depth" : 25 * mm});
        }
        {
            var Q0;
            Q0=makeQuery(id+"F3.boolean.opBoolean","COPY",EDGE,{"derivedFrom":makeQuery(id+"F3.opExtrude","CAP_EDGE",EDGE,{"disambiguationData":[OSD([sQuery(id+"F0.wireOp",EDGE,"E25.6")])],"isStart":false})});
            var Q1;
            Q1=makeQuery(id+"F8.boolean.opBoolean","INTERSECT",EDGE,{"derivedFrom":[makeQuery(id+"F5.opExtrude","SWEPT_FACE",FACE,{"disambiguationData":[OSD([sQuery(id+"F4.wireOp",EDGE,"E30")])]}),makeQuery(id+"F8.opExtrude","CAP_FACE",FACE,{"disambiguationData":[OSD([sQuery(id+"F7.wireOp",EDGE,"E67")])],"isStart":false})]});
            var Q2;
            Q2=makeQuery(id+"F8.boolean.opBoolean","INTERSECT",EDGE,{"disambiguationData":[OD(1.0)],"derivedFrom":[makeQuery(id+"F5.opExtrude","SWEPT_FACE",FACE,{"disambiguationData":[OSD([sQuery(id+"F4.wireOp",EDGE,"E30")])]}),makeQuery(id+"F8.opExtrude","SWEPT_FACE",FACE,{"disambiguationData":[OSD([sQuery(id+"F7.wireOp",EDGE,"E67")])]})]});
            var Q3;
            {var subQ0=sQuery(id+"F4.wireOp",EDGE,"E30");Q3=makeQuery(id+"F8.boolean.opBoolean","SPLIT",EDGE,{"disambiguationData":[TD([makeQuery(id+"F5.opExtrude","SWEPT_FACE",FACE,{"disambiguationData":[OSD([sQuery(id+"F4.wireOp",EDGE,"E35.filletArc")])]})])],"derivedFrom":makeQuery(id+"F5.opExtrude","CAP_EDGE",EDGE,{"disambiguationData":[OSD([subQ0])],"isStart":false})});}
            var Q4;
            {var subQ0=sQuery(id+"F0.wireOp",EDGE,"E25.7");var subQ1=sQuery(id+"F0.wireOp",EDGE,"E25.1");var subQ2=sQuery(id+"F0.wireOp",EDGE,"E25.6");var subQ3=sQuery(id+"F0.wireOp",EDGE,"E25.5");var subQ4=sQuery(id+"F0.wireOp",EDGE,"E25.4");var subQ5=sQuery(id+"F0.wireOp",EDGE,"E25.0");var subQ6=sQuery(id+"F0.wireOp",EDGE,"E25.2");var subQ7=sQuery(id+"F0.wireOp",EDGE,"E25.3");Q4=makeQuery(id+"F8.boolean.opBoolean","INTERSECT",EDGE,{"derivedFrom":[makeQuery(id+"F5.boolean.opBoolean","SPLIT",FACE,{"disambiguationData":[TD([makeQuery(id+"F2.opExtrude","SWEPT_FACE",FACE,{"disambiguationData":[OSD([subQ5])]})])],"derivedFrom":makeQuery(id+"F3.boolean.opBoolean","COPY",FACE,{"derivedFrom":makeQuery(id+"F3.opExtrude","CAP_FACE",FACE,{"disambiguationData":[OSD([subQ5,subQ1,subQ6,subQ7,subQ4,subQ3,subQ2,subQ0])],"isStart":false})})}),makeQuery(id+"F8.opExtrude","SWEPT_FACE",FACE,{"disambiguationData":[OSD([sQuery(id+"F7.wireOp",EDGE,"E67")])]})]});}
            var Q5;
            Q5=makeQuery(id+"F8.boolean.opBoolean","INTERSECT",EDGE,{"disambiguationData":[OD(0.0)],"derivedFrom":[makeQuery(id+"F5.opExtrude","SWEPT_FACE",FACE,{"disambiguationData":[OSD([sQuery(id+"F4.wireOp",EDGE,"E30")])]}),makeQuery(id+"F8.opExtrude","SWEPT_FACE",FACE,{"disambiguationData":[OSD([sQuery(id+"F7.wireOp",EDGE,"E67")])]})]});
            fillet(context, id + "F14", {"entities" : qUnion([Q0, Q1, Q2, Q3, Q4, Q5]), "radius" : 3 * mm, "tangentPropagation" : true, "allowEdgeOverflow" : false});
        }
        {
            var Q0;
            Q0=makeQuery(id+"F1.opExtrude","CAP_EDGE",EDGE,{"disambiguationData":[OSD([sQuery(id+"F0.wireOp",EDGE,"E1.bottom")])],"isStart":false});
            fillet(context, id + "F15", {"entities" : qUnion([Q0]), "radius" : 2 * mm, "tangentPropagation" : true, "allowEdgeOverflow" : false});
        }
        {
            var Q0;
            {var subQ0=sQuery(id+"F0.wireOp",EDGE,"E21.filletArc");var subQ1=sQuery(id+"F0.wireOp",EDGE,"E7");var subQ2=sQuery(id+"F0.wireOp",EDGE,"E6");var subQ3=sQuery(id+"F0.wireOp",EDGE,"E5");var subQ4=sQuery(id+"F0.wireOp",EDGE,"E4");var subQ5=sQuery(id+"F0.wireOp",EDGE,"E22.filletArc");var subQ6=sQuery(id+"F0.wireOp",EDGE,"E1.bottom");var subQ7=sQuery(id+"F0.wireOp",EDGE,"E1.right");var subQ8=sQuery(id+"F0.wireOp",EDGE,"E1.top");var subQ9=sQuery(id+"F0.wireOp",EDGE,"E1.left");var subQ10=sQuery(id+"F0.wireOp",EDGE,"E23.filletArc");var subQ11=sQuery(id+"F0.wireOp",EDGE,"E24.filletArc");Q0=makeQuery(id+"F2.boolean.opBoolean","SPLIT",FACE,{"disambiguationData":[TD([makeQuery(id+"F1.opExtrude","SWEPT_FACE",FACE,{"disambiguationData":[OSD([subQ6])]})])],"derivedFrom":makeQuery(id+"F1.opExtrude","CAP_FACE",FACE,{"disambiguationData":[OSD([subQ6,subQ8,subQ9,subQ7,subQ4,subQ3,subQ2,subQ1,subQ0,subQ5,subQ10,subQ11])],"isStart":true})});}
            var sketch = newSketch(context, id + "F16", { "sketchPlane" : qUnion([Q0])});
            skLineSegment(sketch, "E79", {"start": v(0, 74.25) * mm, "end": v(0, 104.25) * mm, "construction": true});
            skArc(sketch, "E80", {"start": v(15, 104.25) * mm, "mid": v(0, 119.25) * mm, "end": v(-15, 104.25) * mm});
            skLineSegment(sketch, "E81", {"start": v(15, 104.25) * mm, "end": v(15, 92.25) * mm});
            skLineSegment(sketch, "E82", {"start": v(-15, 104.25) * mm, "end": v(-15, 92.25) * mm});
            skLineSegment(sketch, "E83", {"start": v(15, 92.25) * mm, "end": v(33, 74.25) * mm});
            skLineSegment(sketch, "E84", {"start": v(-15, 92.25) * mm, "end": v(-33, 74.25) * mm});
            skCircle(sketch, "E85", {"center": v(0, 104.25) * mm, "radius": 6 * mm});
            skLineSegment(sketch, "E86", {"start": v(-74.25, 0) * mm, "end": v(74.25, 0) * mm, "construction": true});
            skLineSegment(sketch, "E87.MirrorCS", {"start": v(0, -74.25) * mm, "end": v(0, -104.25) * mm, "construction": true});
            skArc(sketch, "E88.MirrorCS", {"start": v(15, -104.25) * mm, "mid": v(0, -119.25) * mm, "end": v(-15, -104.25) * mm});
            skLineSegment(sketch, "E89.MirrorCS", {"start": v(15, -104.25) * mm, "end": v(15, -92.25) * mm});
            skLineSegment(sketch, "E90.MirrorCS", {"start": v(-15, -104.25) * mm, "end": v(-15, -92.25) * mm});
            skCircle(sketch, "E91.MirrorC", {"center": v(0, -104.25) * mm, "radius": 6 * mm});
            skLineSegment(sketch, "E92.MirrorCS", {"start": v(-15, -92.25) * mm, "end": v(-33, -74.25) * mm});
            skLineSegment(sketch, "E93.MirrorCS", {"start": v(15, -92.25) * mm, "end": v(33, -74.25) * mm});
            skSolve(sketch);
        }
        {
            var Q0;
            Q0=makeQuery(id+"F16.imprint","IMPRINT",FACE,{"disambiguationData":[TD([[makeQuery(id+"F16.imprint","IMPRINT",EDGE,{"derivedFrom":sQuery(id+"F16.wireOp",EDGE,"E80")}),1.0]])]});
            var Q1;
            Q1=makeQuery(id+"F16.imprint","IMPRINT",FACE,{"disambiguationData":[TD([[makeQuery(id+"F16.imprint","IMPRINT",EDGE,{"derivedFrom":makeQuery(id+"F1.opExtrude","CAP_EDGE",EDGE,{"disambiguationData":[OSD([sQuery(id+"F0.wireOp",EDGE,"E1.left")])],"isStart":true})}),-1.0]])]});
            var Q2;
            Q2=makeQuery(id+"F16.imprint","IMPRINT",FACE,{"disambiguationData":[TD([[makeQuery(id+"F16.imprint","IMPRINT",EDGE,{"derivedFrom":sQuery(id+"F16.wireOp",EDGE,"E88.MirrorCS")}),-1.0]])]});
            var Q3;
            Q3=makeQuery(id+"F2.opExtrude","CAP_FACE",FACE,{"disambiguationData":[OSD([sQuery(id+"F0.wireOp",EDGE,"E12"),sQuery(id+"F0.wireOp",EDGE,"E13"),sQuery(id+"F0.wireOp",EDGE,"E14"),sQuery(id+"F0.wireOp",EDGE,"E15"),sQuery(id+"F0.wireOp",EDGE,"E17.filletArc"),sQuery(id+"F0.wireOp",EDGE,"E18.filletArc"),sQuery(id+"F0.wireOp",EDGE,"E19.filletArc"),sQuery(id+"F0.wireOp",EDGE,"E20.filletArc"),sQuery(id+"F0.wireOp",EDGE,"E25.0"),sQuery(id+"F0.wireOp",EDGE,"E25.1"),sQuery(id+"F0.wireOp",EDGE,"E25.2"),sQuery(id+"F0.wireOp",EDGE,"E25.3"),sQuery(id+"F0.wireOp",EDGE,"E25.4"),sQuery(id+"F0.wireOp",EDGE,"E25.5"),sQuery(id+"F0.wireOp",EDGE,"E25.6"),sQuery(id+"F0.wireOp",EDGE,"E25.7")])],"isStart":false});
            extrude(context, id + "F17", {"entities" : qUnion([Q0, Q1, Q2]), "endBound" : BoundingType.UP_TO_SURFACE, "endBoundEntityFace" : qUnion([Q3]), "depth" : 25 * mm});
        }
    });
